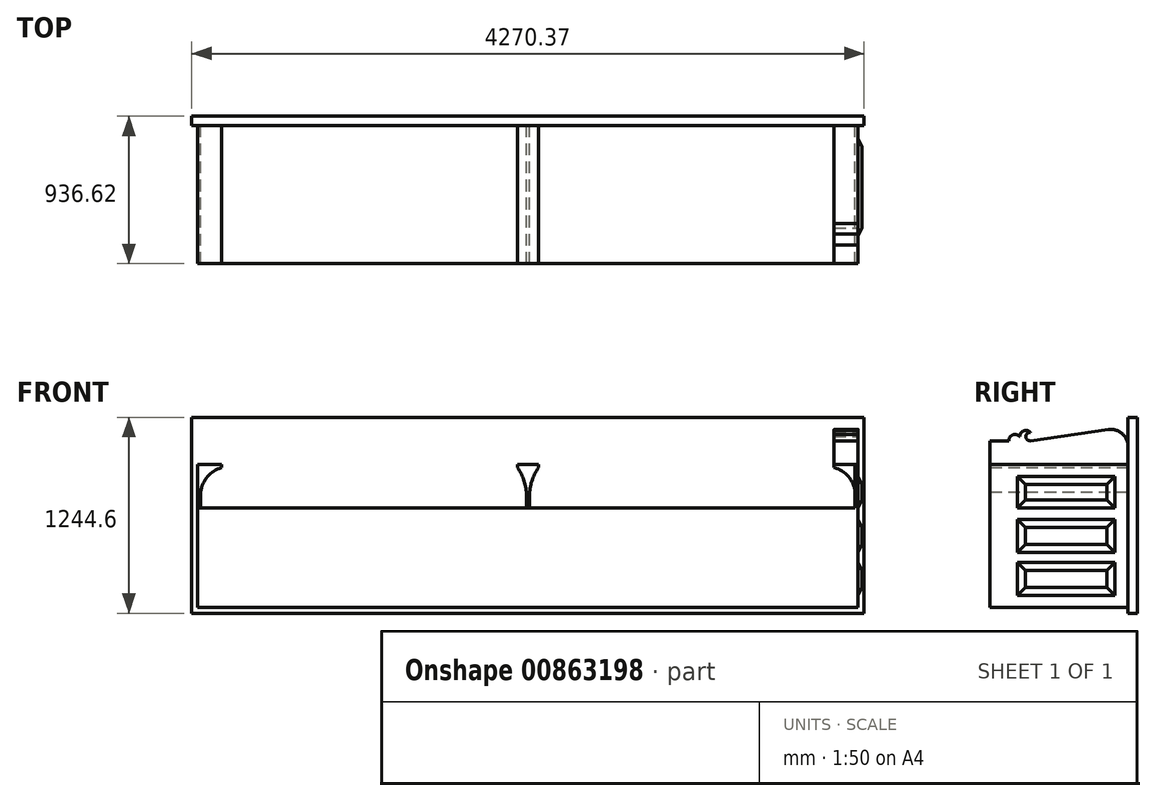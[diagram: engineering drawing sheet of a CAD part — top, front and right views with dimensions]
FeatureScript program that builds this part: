
annotation { "Feature Type Name" : "Feature", "Feature Type Description" : "" }
export const myFeature = defineFeature(function(context is Context, id is Id, definition is map)
    precondition{}
    {
        {
            var Q0;
            Q0=qCreatedBy(makeId("Front.planeOp"),FACE);
            var sketch = newSketch(context, id + "F0", { "sketchPlane" : qUnion([Q0])});
            skLineSegment(sketch, "E0.bottom", {"start": v(0, 0) * mm, "end": v(-4194.18, 0) * mm});
            skLineSegment(sketch, "E0.top", {"start": v(0, 631.83) * mm, "end": v(-4194.18, 631.82) * mm});
            skLineSegment(sketch, "E0.left", {"start": v(0, 0) * mm, "end": v(0, 631.83) * mm});
            skLineSegment(sketch, "E0.right", {"start": v(-4194.18, 0) * mm, "end": v(-4194.18, 631.82) * mm});
            skSolve(sketch);
        }
        {
            var Q0;
            Q0=makeQuery(id+"F0.imprint","IMPRINT",FACE,{"disambiguationData":[TD([[makeQuery(id+"F0.imprint","IMPRINT",EDGE,{"derivedFrom":sQuery(id+"F0.wireOp",EDGE,"E0.bottom")}),-1.0]])]});
            extrude(context, id + "F1", {"entities" : qUnion([Q0]), "depth" : 876.3 * mm, "offsetDistance" : 25.4 * mm});
        }
        {
            var Q0;
            Q0=qCreatedBy(makeId("Top.planeOp"),FACE);
            var sketch = newSketch(context, id + "F2", { "sketchPlane" : qUnion([Q0])});
            skLineSegment(sketch, "E1.bottom", {"start": v(38.1, 0) * mm, "end": v(-4232.28, 0) * mm});
            skLineSegment(sketch, "E1.top", {"start": v(38.1, 60.32) * mm, "end": v(-4232.28, 60.32) * mm});
            skLineSegment(sketch, "E1.left", {"start": v(38.1, 0) * mm, "end": v(38.1, 60.32) * mm});
            skLineSegment(sketch, "E1.right", {"start": v(-4232.28, 0) * mm, "end": v(-4232.28, 60.32) * mm});
            skSolve(sketch);
        }
        {
            var Q0;
            Q0=makeQuery(id+"F2.imprint","IMPRINT",FACE,{"disambiguationData":[TD([[makeQuery(id+"F2.imprint","IMPRINT",EDGE,{"derivedFrom":sQuery(id+"F2.wireOp",EDGE,"E1.bottom")}),-1.0]])]});
            extrude(context, id + "F3", {"entities" : qUnion([Q0]), "operationType" : NewBodyOperationType.ADD, "depth" : 1206.5 * mm, "offsetDistance" : 25.4 * mm});
        }
        {
            var Q0;
            Q0=makeQuery(id+"F2.imprint","IMPRINT",FACE,{"disambiguationData":[TD([[makeQuery(id+"F2.imprint","IMPRINT",EDGE,{"derivedFrom":sQuery(id+"F2.wireOp",EDGE,"E1.bottom")}),-1.0]])]});
            extrude(context, id + "F4", {"entities" : qUnion([Q0]), "operationType" : NewBodyOperationType.ADD, "oppositeDirection" : true, "depth" : 38.1 * mm, "offsetDistance" : 25.4 * mm});
        }
        {
            var Q0;
            Q0=makeQuery(id+"F1.opExtrude","SWEPT_FACE",FACE,{"disambiguationData":[OSD([sQuery(id+"F0.wireOp",EDGE,"E0.left")])]});
            var sketch = newSketch(context, id + "F5", { "sketchPlane" : qUnion([Q0])});
            skLineSegment(sketch, "E2.bottom", {"start": v(-82.55, 283.37) * mm, "end": v(-701.68, 283.37) * mm});
            skLineSegment(sketch, "E2.top", {"start": v(-82.55, 74.61) * mm, "end": v(-701.67, 74.61) * mm});
            skLineSegment(sketch, "E2.left", {"start": v(-82.55, 283.37) * mm, "end": v(-82.55, 74.61) * mm});
            skLineSegment(sketch, "E2.right", {"start": v(-701.68, 283.37) * mm, "end": v(-701.68, 74.61) * mm});
            skLineSegment(sketch, "E3.bottom", {"start": v(-82.55, 348.46) * mm, "end": v(-701.68, 348.46) * mm});
            skLineSegment(sketch, "E3.top", {"start": v(-82.55, 557.21) * mm, "end": v(-701.68, 557.21) * mm});
            skLineSegment(sketch, "E3.left", {"start": v(-82.55, 348.46) * mm, "end": v(-82.55, 557.21) * mm});
            skLineSegment(sketch, "E3.right", {"start": v(-701.68, 348.46) * mm, "end": v(-701.68, 557.21) * mm});
            skLineSegment(sketch, "E4.bottom", {"start": v(-82.55, 622.3) * mm, "end": v(-701.67, 622.3) * mm});
            skLineSegment(sketch, "E4.top", {"start": v(-82.55, 831.06) * mm, "end": v(-701.67, 831.06) * mm});
            skLineSegment(sketch, "E4.left", {"start": v(-82.55, 622.3) * mm, "end": v(-82.55, 831.06) * mm});
            skLineSegment(sketch, "E4.right", {"start": v(-701.68, 622.3) * mm, "end": v(-701.68, 831.06) * mm});
            skSolve(sketch);
        }
        {
            var Q0;
            Q0=makeQuery(id+"F1.opExtrude","SWEPT_FACE",FACE,{"disambiguationData":[OSD([sQuery(id+"F0.wireOp",EDGE,"E0.top")])]});
            var sketch = newSketch(context, id + "F6", { "sketchPlane" : qUnion([Q0])});
            skLineSegment(sketch, "E5.bottom", {"start": v(0, 0) * mm, "end": v(-19.05, 0) * mm});
            skLineSegment(sketch, "E5.top", {"start": v(0, -876.3) * mm, "end": v(-19.05, -876.3) * mm});
            skLineSegment(sketch, "E5.left", {"start": v(0, 0) * mm, "end": v(0, -876.3) * mm});
            skLineSegment(sketch, "E5.right", {"start": v(-19.05, 0) * mm, "end": v(-19.05, -876.3) * mm});
            skSolve(sketch);
        }
        {
            var Q0;
            Q0=makeQuery(id+"F6.imprint","IMPRINT",FACE,{"disambiguationData":[TD([[makeQuery(id+"F6.imprint","IMPRINT",EDGE,{"derivedFrom":sQuery(id+"F6.wireOp",EDGE,"E5.bottom")}),1.0]])]});
            extrude(context, id + "F7", {"entities" : qUnion([Q0]), "operationType" : NewBodyOperationType.ADD, "depth" : 273.8 * mm, "offsetDistance" : 25.4 * mm});
        }
        {
            var Q0;
            Q0=makeQuery(id+"F7.boolean.opBoolean","MERGE",FACE,{"derivedFrom":[makeQuery(id+"F1.opExtrude","SWEPT_FACE",FACE,{"disambiguationData":[OSD([sQuery(id+"F0.wireOp",EDGE,"E0.left")])]}),makeQuery(id+"F7.opExtrude","SWEPT_FACE",FACE,{"disambiguationData":[OSD([sQuery(id+"F6.wireOp",EDGE,"E5.left")])]})]});
            var sketch = newSketch(context, id + "F8", { "sketchPlane" : qUnion([Q0])});
            skLineSegment(sketch, "E6.bottom", {"start": v(0, 905.64) * mm, "end": v(-876.3, 905.64) * mm});
            skLineSegment(sketch, "E6.top", {"start": v(0, 1134.24) * mm, "end": v(-876.3, 1134.24) * mm});
            skLineSegment(sketch, "E6.left", {"start": v(0, 905.64) * mm, "end": v(0, 1134.24) * mm});
            skLineSegment(sketch, "E6.right", {"start": v(-876.3, 905.64) * mm, "end": v(-876.3, 1134.24) * mm});
            skCircle(sketch, "E7", {"center": v(-110.26, 1019.94) * mm, "radius": 110.26 * mm});
            skPoint(sketch, "E7.centerSnap0", {"position": v(0, 1019.94) * mm});
            skLineSegment(sketch, "E8", {"start": v(-126.1, 1129.05) * mm, "end": v(-619.42, 1057.44) * mm});
            skArc(sketch, "E9", {"start": v(-619.42, 1109.6) * mm, "mid": v(-649.56, 1083.52) * mm, "end": v(-619.42, 1057.44) * mm});
            skArc(sketch, "E10", {"start": v(-619.42, 1109.6) * mm, "mid": v(-675.04, 1113.06) * mm, "end": v(-678.5, 1057.44) * mm});
            skCircle(sketch, "E11", {"center": v(-718.21, 1057.44) * mm, "radius": 39.71 * mm});
            skLineSegment(sketch, "E12", {"start": v(-718.21, 1057.44) * mm, "end": v(-718.21, 1097.15) * mm, "construction": true});
            skLineSegment(sketch, "E13", {"start": v(-757.93, 1057.44) * mm, "end": v(-876.3, 1057.44) * mm});
            skSolve(sketch);
        }
        {
            var Q0;
            {var subQ1=sQuery(id+"F8.wireOp",EDGE,"E6.bottom");Q0=makeQuery(id+"F8.imprint","IMPRINT",FACE,{"disambiguationData":[TD([[makeQuery(id+"F8.imprint","IMPRINT",EDGE,{"derivedFrom":subQ1}),1.0]])]});}
            var Q1;
            {var subQ0=sQuery(id+"F8.wireOp",EDGE,"E7");var subQ1=makeQuery(id+"F8.imprint","INTERSECT",VERTEX,{"derivedFrom":[subQ0,sQuery(id+"F8.wireOp",EDGE,"E8")]});Q1=makeQuery(id+"F8.imprint","IMPRINT",FACE,{"disambiguationData":[TD([[makeQuery(id+"F8.imprint","IMPRINT",EDGE,{"disambiguationData":[TD([[subQ1,1.0]])],"derivedFrom":subQ0}),1.0]])]});}
            extrude(context, id + "F9", {"entities" : qUnion([Q0, Q1]), "oppositeDirection" : true, "depth" : 152.4 * mm, "offsetDistance" : 25.4 * mm});
        }
        {
            var Q0;
            {var subQ0=sQuery(id+"F8.wireOp",EDGE,"E11");var subQ1=sQuery(id+"F8.wireOp",EDGE,"E10");var subQ2=makeQuery(id+"F8.imprint","INTERSECT",VERTEX,{"disambiguationData":[OD(0.0)],"derivedFrom":[subQ1,subQ0]});Q0=makeQuery(id+"F8.imprint","IMPRINT",FACE,{"disambiguationData":[TD([[makeQuery(id+"F8.imprint","IMPRINT",EDGE,{"disambiguationData":[TD([[subQ2,1.0]])],"derivedFrom":subQ1}),-1.0]])]});}
            var Q1;
            {var subQ0=sQuery(id+"F8.wireOp",EDGE,"E11");var subQ1=sQuery(id+"F8.wireOp",EDGE,"E10");var subQ2=makeQuery(id+"F8.imprint","INTERSECT",VERTEX,{"disambiguationData":[OD(0.0)],"derivedFrom":[subQ1,subQ0]});Q1=makeQuery(id+"F8.imprint","IMPRINT",FACE,{"disambiguationData":[TD([[makeQuery(id+"F8.imprint","IMPRINT",EDGE,{"disambiguationData":[TD([[subQ2,1.0]])],"derivedFrom":subQ1}),1.0]])]});}
            var Q2;
            Q2=makeQuery(id+"F9.opExtrude","CAP_FACE",FACE,{"disambiguationData":[OSD([sQuery(id+"F8.wireOp",EDGE,"E6.bottom"),sQuery(id+"F8.wireOp",EDGE,"E6.left"),sQuery(id+"F8.wireOp",EDGE,"E6.right"),sQuery(id+"F8.wireOp",EDGE,"E7"),sQuery(id+"F8.wireOp",EDGE,"E8"),sQuery(id+"F8.wireOp",EDGE,"E9"),sQuery(id+"F8.wireOp",EDGE,"E10"),sQuery(id+"F8.wireOp",EDGE,"E11"),sQuery(id+"F8.wireOp",EDGE,"E13")])],"isStart":false});
            extrude(context, id + "F10", {"entities" : qUnion([Q0, Q1]), "operationType" : NewBodyOperationType.ADD, "endBound" : BoundingType.UP_TO_SURFACE, "oppositeDirection" : true, "depth" : 25.4 * mm, "endBoundEntityFace" : qUnion([Q2]), "offsetDistance" : 25.4 * mm});
        }
        {
            var Q0;
            {var subQ0=sQuery(id+"F5.wireOp",EDGE,"E4.top");Q0=makeQuery(id+"F5.imprint","IMPRINT",FACE,{"disambiguationData":[TD([[makeQuery(id+"F5.imprint","IMPRINT",EDGE,{"derivedFrom":subQ0}),1.0]])]});}
            cPlane(context, id + "F11", {"entities" : qUnion([Q0]), "cplaneType" : CPlaneType.OFFSET, "offset" : 25.4 * mm, "width" : 152.4 * mm, "height" : 152.4 * mm});
        }
        {
            var Q0;
            Q0=qCreatedBy(id+"F11.planeOp",FACE);
            var sketch = newSketch(context, id + "F12", { "sketchPlane" : qUnion([Q0])});
            skLineSegment(sketch, "E14.0", {"start": v(-650.88, 780.26) * mm, "end": v(-650.88, 682.63) * mm});
            skLineSegment(sketch, "E14.1", {"start": v(-133.35, 780.26) * mm, "end": v(-650.88, 780.26) * mm});
            skLineSegment(sketch, "E14.2", {"start": v(-133.35, 682.63) * mm, "end": v(-133.35, 780.26) * mm});
            skLineSegment(sketch, "E14.3", {"start": v(-650.88, 682.63) * mm, "end": v(-133.35, 682.63) * mm});
            skLineSegment(sketch, "E15.0", {"start": v(-133.35, 399.26) * mm, "end": v(-133.35, 506.41) * mm});
            skLineSegment(sketch, "E15.1", {"start": v(-650.88, 399.26) * mm, "end": v(-133.35, 399.26) * mm});
            skLineSegment(sketch, "E15.2", {"start": v(-650.88, 506.41) * mm, "end": v(-650.88, 399.26) * mm});
            skLineSegment(sketch, "E15.3", {"start": v(-133.35, 506.41) * mm, "end": v(-650.88, 506.41) * mm});
            skLineSegment(sketch, "E16.0", {"start": v(-650.88, 125.41) * mm, "end": v(-133.35, 125.41) * mm});
            skLineSegment(sketch, "E16.1", {"start": v(-650.88, 232.57) * mm, "end": v(-650.88, 125.41) * mm});
            skLineSegment(sketch, "E16.2", {"start": v(-133.35, 232.57) * mm, "end": v(-650.88, 232.57) * mm});
            skLineSegment(sketch, "E16.3", {"start": v(-133.35, 125.41) * mm, "end": v(-133.35, 232.57) * mm});
            skSolve(sketch);
        }
        {
            var Q1;
            Q1=makeQuery(id+"F5.imprint","IMPRINT",FACE,{"disambiguationData":[TD([[makeQuery(id+"F5.imprint","IMPRINT",EDGE,{"derivedFrom":sQuery(id+"F5.wireOp",EDGE,"E3.bottom")}),-1.0]])]});
            var Q2;
            Q2=makeQuery(id+"F12.imprint","IMPRINT",FACE,{"disambiguationData":[TD([[makeQuery(id+"F12.imprint","IMPRINT",EDGE,{"derivedFrom":sQuery(id+"F12.wireOp",EDGE,"E15.0")}),1.0]])]});
            loft(context, id + "F13", {"operationType" : NewBodyOperationType.ADD, "sheetProfilesArray" : [{ "sheetProfileEntities" : qUnion([Q1]) }, { "sheetProfileEntities" : qUnion([Q2]) }]});
        }
        {
            var Q1;
            Q1=makeQuery(id+"F5.imprint","IMPRINT",FACE,{"disambiguationData":[TD([[makeQuery(id+"F5.imprint","IMPRINT",EDGE,{"derivedFrom":sQuery(id+"F5.wireOp",EDGE,"E2.bottom")}),1.0]])]});
            var Q2;
            Q2=makeQuery(id+"F12.imprint","IMPRINT",FACE,{"disambiguationData":[TD([[makeQuery(id+"F12.imprint","IMPRINT",EDGE,{"derivedFrom":sQuery(id+"F12.wireOp",EDGE,"E16.0")}),1.0]])]});
            loft(context, id + "F14", {"operationType" : NewBodyOperationType.ADD, "sheetProfilesArray" : [{ "sheetProfileEntities" : qUnion([Q1]) }, { "sheetProfileEntities" : qUnion([Q2]) }]});
        }
        {
            var Q1;
            {var subQ0=sQuery(id+"F5.wireOp",EDGE,"E4.top");Q1=makeQuery(id+"F5.imprint","IMPRINT",FACE,{"disambiguationData":[TD([[makeQuery(id+"F5.imprint","IMPRINT",EDGE,{"derivedFrom":subQ0}),1.0]])]});}
            var Q2;
            Q2=makeQuery(id+"F12.imprint","IMPRINT",FACE,{"disambiguationData":[TD([[makeQuery(id+"F12.imprint","IMPRINT",EDGE,{"derivedFrom":sQuery(id+"F12.wireOp",EDGE,"E14.0")}),1.0]])]});
            loft(context, id + "F15", {"operationType" : NewBodyOperationType.ADD, "sheetProfilesArray" : [{ "sheetProfileEntities" : qUnion([Q1]) }, { "sheetProfileEntities" : qUnion([Q2]) }]});
        }
        {
            var Q0;
            {var subQ0=sQuery(id+"F2.wireOp",EDGE,"E1.bottom");Q0=makeQuery(id+"F4.boolean.opBoolean","MERGE",FACE,{"derivedFrom":[makeQuery(id+"F3.opExtrude","SWEPT_FACE",FACE,{"disambiguationData":[OSD([subQ0])]}),makeQuery(id+"F4.opExtrude","SWEPT_FACE",FACE,{"disambiguationData":[OSD([subQ0])]})]});}
            var sketch = newSketch(context, id + "F16", { "sketchPlane" : qUnion([Q0])});
            skLineSegment(sketch, "E17.bottom", {"start": v(-19.05, 905.64) * mm, "end": v(-152.4, 905.64) * mm});
            skLineSegment(sketch, "E17.top", {"start": v(-19.05, 886.59) * mm, "end": v(-152.4, 886.59) * mm});
            skLineSegment(sketch, "E17.left", {"start": v(-19.05, 905.64) * mm, "end": v(-19.05, 886.59) * mm});
            skLineSegment(sketch, "E17.right", {"start": v(-152.4, 905.64) * mm, "end": v(-152.4, 886.59) * mm});
            skArc(sketch, "E18", {"start": v(-19.05, 732.1) * mm, "mid": v(-62.13, 829.71) * mm, "end": v(-152.4, 886.59) * mm});
            skLineSegment(sketch, "E19", {"start": v(-2097.09, 1206.5) * mm, "end": v(-2097.09, 631.82) * mm, "construction": true});
            skLineSegment(sketch, "E20.bottom", {"start": v(-2087.56, 631.82) * mm, "end": v(-2106.61, 631.82) * mm});
            skLineSegment(sketch, "E20.top", {"start": v(-2087.56, 886.59) * mm, "end": v(-2106.61, 886.59) * mm});
            skLineSegment(sketch, "E20.left", {"start": v(-2087.56, 631.82) * mm, "end": v(-2087.56, 886.59) * mm});
            skLineSegment(sketch, "E20.right", {"start": v(-2106.61, 631.82) * mm, "end": v(-2106.61, 886.59) * mm});
            skPoint(sketch, "E20.middle", {"position": v(-2097.09, 759.2) * mm});
            skLineSegment(sketch, "E21.bottom", {"start": v(-2030.41, 886.59) * mm, "end": v(-2163.76, 886.59) * mm});
            skLineSegment(sketch, "E21.top", {"start": v(-2030.41, 905.64) * mm, "end": v(-2163.76, 905.64) * mm});
            skLineSegment(sketch, "E21.left", {"start": v(-2030.41, 886.59) * mm, "end": v(-2030.41, 905.64) * mm});
            skLineSegment(sketch, "E21.right", {"start": v(-2163.76, 886.59) * mm, "end": v(-2163.76, 905.64) * mm});
            skPoint(sketch, "E21.middle", {"position": v(-2097.09, 896.11) * mm});
            skArc(sketch, "E22", {"start": v(-2030.41, 886.59) * mm, "mid": v(-2072.93, 801.57) * mm, "end": v(-2087.56, 707.64) * mm});
            skArc(sketch, "E23.MirrorCS", {"start": v(-2163.76, 886.59) * mm, "mid": v(-2121.25, 801.57) * mm, "end": v(-2106.61, 707.64) * mm});
            skLineSegment(sketch, "E24.MirrorCS", {"start": v(-4175.12, 905.64) * mm, "end": v(-4041.78, 905.64) * mm});
            skLineSegment(sketch, "E25.MirrorCS", {"start": v(-4175.12, 886.59) * mm, "end": v(-4041.78, 886.59) * mm});
            skLineSegment(sketch, "E26.MirrorCS", {"start": v(-4041.78, 905.64) * mm, "end": v(-4041.78, 886.59) * mm});
            skArc(sketch, "E27.MirrorCS", {"start": v(-4175.12, 732.1) * mm, "mid": v(-4132.04, 829.71) * mm, "end": v(-4041.78, 886.59) * mm});
            skLineSegment(sketch, "E28.bottom", {"start": v(-4194.18, 631.82) * mm, "end": v(-4175.12, 631.82) * mm});
            skLineSegment(sketch, "E28.top", {"start": v(-4194.18, 905.64) * mm, "end": v(-4175.12, 905.64) * mm});
            skLineSegment(sketch, "E28.left", {"start": v(-4194.18, 631.82) * mm, "end": v(-4194.18, 905.64) * mm});
            skLineSegment(sketch, "E28.right", {"start": v(-4175.12, 631.82) * mm, "end": v(-4175.12, 905.64) * mm});
            skSolve(sketch);
        }
        {
            var Q0;
            Q0 = qSketchRegion(id + "F16", true);
            var Q1;
            {var subQ0=sQuery(id+"F16.wireOp",EDGE,"E17.top");Q1=makeQuery(id+"F16.imprint","IMPRINT",FACE,{"disambiguationData":[TD([[makeQuery(id+"F16.imprint","IMPRINT",EDGE,{"derivedFrom":subQ0}),1.0]])]});}
            var Q2;
            Q2=makeQuery(id+"F7.boolean.opBoolean","MERGE",FACE,{"derivedFrom":[makeQuery(id+"F1.opExtrude","CAP_FACE",FACE,{"disambiguationData":[OSD([sQuery(id+"F0.wireOp",EDGE,"E0.bottom"),sQuery(id+"F0.wireOp",EDGE,"E0.top"),sQuery(id+"F0.wireOp",EDGE,"E0.left"),sQuery(id+"F0.wireOp",EDGE,"E0.right")])],"isStart":false}),makeQuery(id+"F7.opExtrude","SWEPT_FACE",FACE,{"disambiguationData":[OSD([sQuery(id+"F6.wireOp",EDGE,"E5.top")])]})]});
            extrude(context, id + "F17", {"entities" : qUnion([Q0, Q1]), "endBound" : BoundingType.UP_TO_SURFACE, "depth" : 25.4 * mm, "endBoundEntityFace" : qUnion([Q2]), "offsetDistance" : 25.4 * mm});
        }
    });
